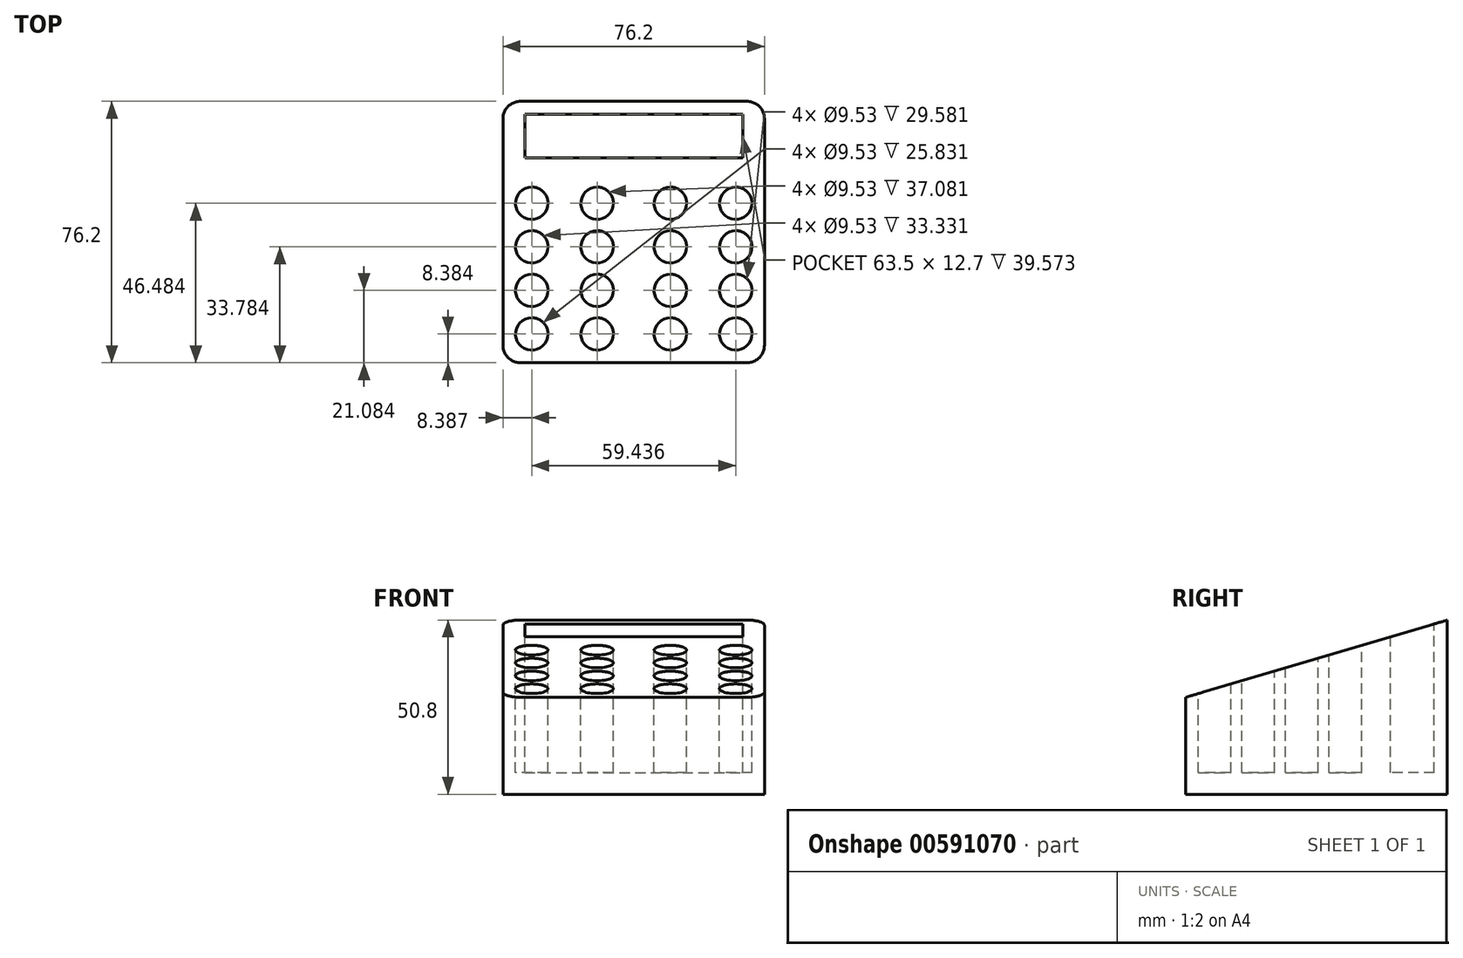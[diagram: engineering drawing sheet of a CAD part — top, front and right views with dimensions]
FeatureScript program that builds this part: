
annotation { "Feature Type Name" : "Feature", "Feature Type Description" : "" }
export const myFeature = defineFeature(function(context is Context, id is Id, definition is map)
    precondition{}
    {
        {
            var Q0;
            Q0=qCreatedBy(makeId("Top.planeOp"),FACE);
            var sketch = newSketch(context, id + "F0", { "sketchPlane" : qUnion([Q0])});
            skLineSegment(sketch, "E0.bottom", {"start": v(33.21, 39.07) * mm, "end": v(-42.99, 39.07) * mm});
            skLineSegment(sketch, "E0.top", {"start": v(33.21, -37.13) * mm, "end": v(-42.99, -37.13) * mm});
            skLineSegment(sketch, "E0.left", {"start": v(33.21, 39.07) * mm, "end": v(33.21, -37.13) * mm});
            skLineSegment(sketch, "E0.right", {"start": v(-42.99, 39.07) * mm, "end": v(-42.99, -37.13) * mm});
            skSolve(sketch);
        }
        {
            var Q0;
            Q0 = qSketchRegion(id + "F0", true);
            extrude(context, id + "F1", {"entities" : qUnion([Q0]), "depth" : 50.8 * mm, "offsetDistance" : 25.4 * mm});
        }
        {
            var Q0;
            Q0=makeQuery(id+"F1.opExtrude","CAP_FACE",FACE,{"disambiguationData":[OSD([sQuery(id+"F0.wireOp",EDGE,"E0.bottom"),sQuery(id+"F0.wireOp",EDGE,"E0.top"),sQuery(id+"F0.wireOp",EDGE,"E0.left"),sQuery(id+"F0.wireOp",EDGE,"E0.right")])],"isStart":false});
            var sketch = newSketch(context, id + "F2", { "sketchPlane" : qUnion([Q0])});
            skCircle(sketch, "E1", {"center": v(-34.6, 9.35) * mm, "radius": 4.76 * mm});
            skCircle(sketch, "E2", {"center": v(-15.55, 9.35) * mm, "radius": 4.76 * mm});
            skCircle(sketch, "E3", {"center": v(-34.6, -3.35) * mm, "radius": 4.76 * mm});
            skCircle(sketch, "E4", {"center": v(-34.6, -16.05) * mm, "radius": 4.76 * mm});
            skCircle(sketch, "E5", {"center": v(-34.6, -28.75) * mm, "radius": 4.76 * mm});
            skCircle(sketch, "E6", {"center": v(-15.55, -3.35) * mm, "radius": 4.76 * mm});
            skCircle(sketch, "E7", {"center": v(-15.55, -16.05) * mm, "radius": 4.76 * mm});
            skCircle(sketch, "E8", {"center": v(-15.55, -28.75) * mm, "radius": 4.76 * mm});
            skCircle(sketch, "E9", {"center": v(5.78, 9.35) * mm, "radius": 4.76 * mm});
            skCircle(sketch, "E10", {"center": v(5.78, -3.35) * mm, "radius": 4.76 * mm});
            skCircle(sketch, "E11", {"center": v(5.78, -16.05) * mm, "radius": 4.76 * mm});
            skCircle(sketch, "E12", {"center": v(5.78, -28.75) * mm, "radius": 4.76 * mm});
            skCircle(sketch, "E13", {"center": v(24.83, 9.35) * mm, "radius": 4.76 * mm});
            skCircle(sketch, "E14", {"center": v(24.83, -3.35) * mm, "radius": 4.76 * mm});
            skCircle(sketch, "E15", {"center": v(24.83, -16.05) * mm, "radius": 4.76 * mm});
            skCircle(sketch, "E16", {"center": v(24.83, -28.75) * mm, "radius": 4.76 * mm});
            skLineSegment(sketch, "E17.bottom", {"start": v(-36.64, 35.26) * mm, "end": v(26.86, 35.26) * mm});
            skLineSegment(sketch, "E17.top", {"start": v(-36.64, 22.56) * mm, "end": v(26.86, 22.56) * mm});
            skLineSegment(sketch, "E17.left", {"start": v(-36.64, 35.26) * mm, "end": v(-36.64, 22.56) * mm});
            skLineSegment(sketch, "E17.right", {"start": v(26.86, 35.26) * mm, "end": v(26.86, 22.56) * mm});
            skSolve(sketch);
        }
        {
            var Q0;
            Q0 = qSketchRegion(id + "F2", true);
            extrude(context, id + "F3", {"entities" : qUnion([Q0]), "operationType" : NewBodyOperationType.REMOVE, "oppositeDirection" : true, "depth" : 44.45 * mm, "offsetDistance" : 25.4 * mm});
        }
        {
            var Q0;
            Q0=makeQuery(id+"F1.opExtrude","SWEPT_FACE",FACE,{"disambiguationData":[OSD([sQuery(id+"F0.wireOp",EDGE,"E0.right")])]});
            var sketch = newSketch(context, id + "F4", { "sketchPlane" : qUnion([Q0])});
            skLineSegment(sketch, "E18.bottom", {"start": v(-39.07, 50.8) * mm, "end": v(37.13, 50.8) * mm});
            skLineSegment(sketch, "E18.right", {"start": v(37.13, 50.8) * mm, "end": v(37.13, 28.3) * mm});
            skLineSegment(sketch, "E19", {"start": v(-39.07, 50.8) * mm, "end": v(37.13, 28.3) * mm});
            skSolve(sketch);
        }
        {
            var Q0;
            Q0 = qSketchRegion(id + "F4", true);
            extrude(context, id + "F5", {"entities" : qUnion([Q0]), "operationType" : NewBodyOperationType.REMOVE, "oppositeDirection" : true, "depth" : 76.2 * mm, "offsetDistance" : 25.4 * mm});
        }
        {
            var Q0;
            Q0=makeQuery(id+"F1.opExtrude","SWEPT_EDGE",EDGE,{"disambiguationData":[OSD([sQuery(id+"F0.wireOp",EDGE,"E0.top"),sQuery(id+"F0.wireOp",EDGE,"E0.left")])]});
            var Q1;
            Q1=makeQuery(id+"F1.opExtrude","SWEPT_EDGE",EDGE,{"disambiguationData":[OSD([sQuery(id+"F0.wireOp",EDGE,"E0.top"),sQuery(id+"F0.wireOp",EDGE,"E0.right")])]});
            var Q2;
            Q2=makeQuery(id+"F1.opExtrude","SWEPT_EDGE",EDGE,{"disambiguationData":[OSD([sQuery(id+"F0.wireOp",EDGE,"E0.bottom"),sQuery(id+"F0.wireOp",EDGE,"E0.left")])]});
            var Q3;
            Q3=makeQuery(id+"F1.opExtrude","SWEPT_EDGE",EDGE,{"disambiguationData":[OSD([sQuery(id+"F0.wireOp",EDGE,"E0.bottom"),sQuery(id+"F0.wireOp",EDGE,"E0.right")])]});
            fillet(context, id + "F6", {"entities" : qUnion([Q0, Q1, Q2, Q3]), "radius" : 5.08 * mm, "tangentPropagation" : true, "allowEdgeOverflow" : false});
        }
    });
